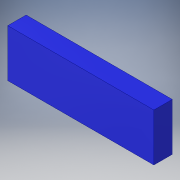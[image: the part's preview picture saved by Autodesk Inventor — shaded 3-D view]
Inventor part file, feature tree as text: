
AUTODESK INVENTOR PART (.ipt)
format: ipt  version: 2019 (Build 230136000, 136)  size: 89,088 bytes
history: native  units: in
note: dims shown in document units (in); Inventor stores cm internally (conversion verified against a paired STEP export)
features: extrude x1, sketch x1
ambient origin geometry x8: Origin, YZ Plane, XZ Plane, XY Plane, X Axis, Y Axis, Z Axis, Center Point
bodies: Solid1 (feature_tree)
feature tree (2):
  extrude  "Extrusion1"  Depth=1.7323in
  sketch  "Sketch1"  dims[d0=5.315in d1=1.7323in d2=0.6693in d3=0.0in]
